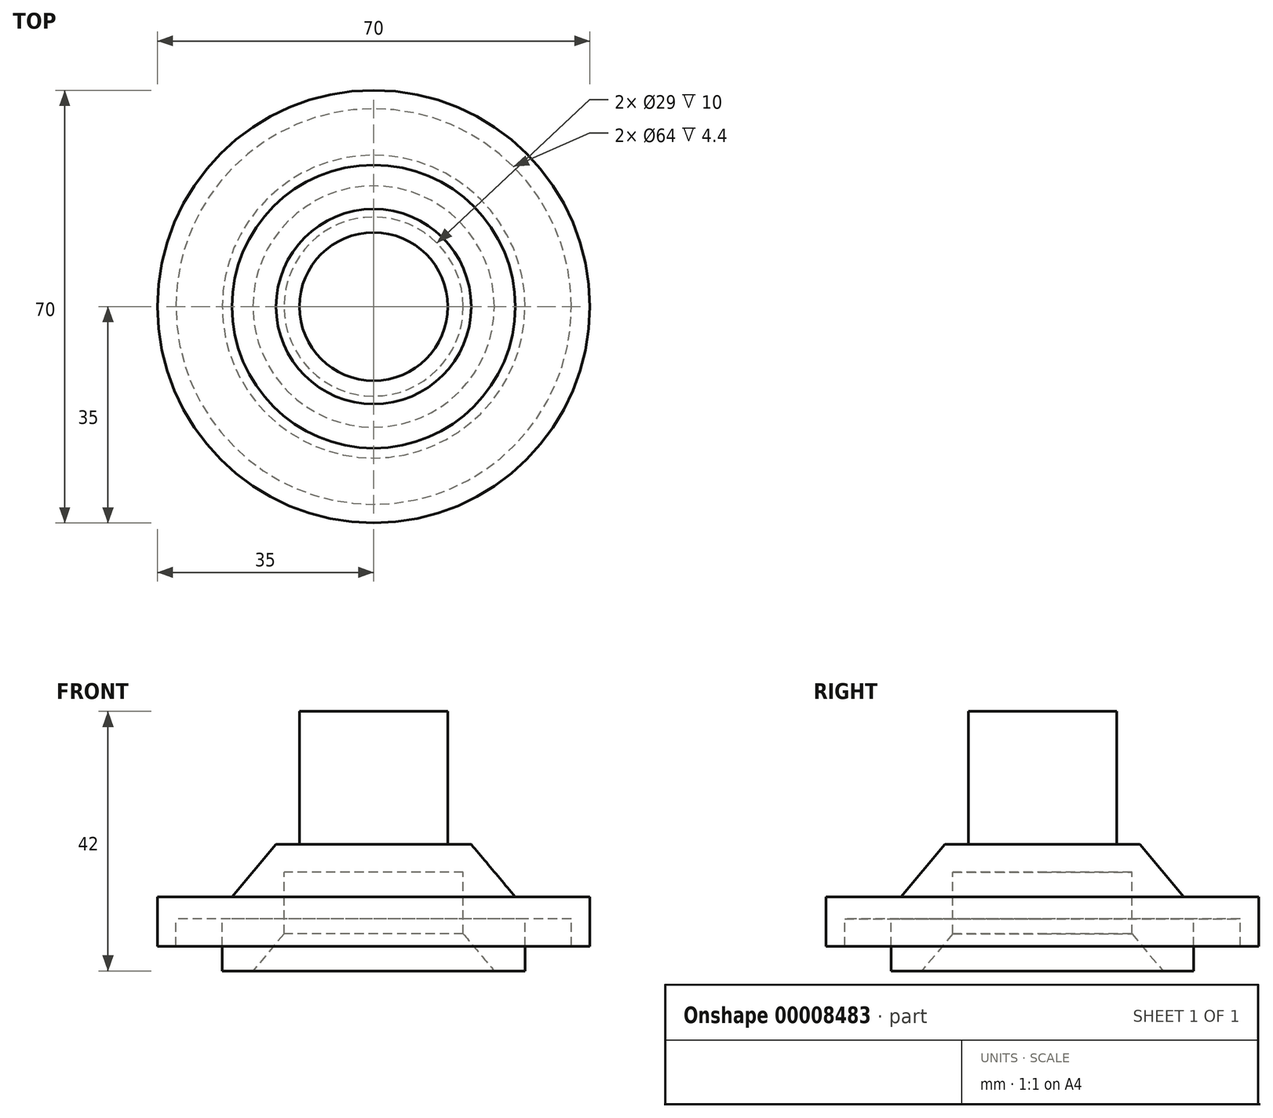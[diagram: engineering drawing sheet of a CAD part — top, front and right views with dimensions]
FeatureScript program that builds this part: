
annotation { "Feature Type Name" : "Feature", "Feature Type Description" : "" }
export const myFeature = defineFeature(function(context is Context, id is Id, definition is map)
    precondition{}
    {
        {
            var Q0;
            Q0=qCreatedBy(makeId("Right.planeOp"),FACE);
            var sketch = newSketch(context, id + "F0", { "sketchPlane" : qUnion([Q0])});
            skLineSegment(sketch, "E0", {"start": v(0, 36) * mm, "end": v(-12, 36) * mm});
            skLineSegment(sketch, "E1", {"start": v(-12, 36) * mm, "end": v(-12, 14.5) * mm});
            skLineSegment(sketch, "E2", {"start": v(-12, 14.5) * mm, "end": v(-15.78, 14.5) * mm});
            skLineSegment(sketch, "E3", {"start": v(-35, -2) * mm, "end": v(-32, -2) * mm});
            skLineSegment(sketch, "E4", {"start": v(-32, -2) * mm, "end": v(-32, 2.4) * mm});
            skLineSegment(sketch, "E5", {"start": v(-32, 2.4) * mm, "end": v(-24.5, 2.4) * mm});
            skLineSegment(sketch, "E6", {"start": v(-24.5, 2.4) * mm, "end": v(-24.5, -6) * mm});
            skLineSegment(sketch, "E7", {"start": v(-24.5, -6) * mm, "end": v(-19.53, -6) * mm});
            skLineSegment(sketch, "E8", {"start": v(-19.53, -6) * mm, "end": v(-14.5, 0) * mm});
            skLineSegment(sketch, "E9", {"start": v(-14.5, 0) * mm, "end": v(-14.5, 10) * mm});
            skLineSegment(sketch, "E10", {"start": v(-14.5, 10) * mm, "end": v(0, 10) * mm});
            skLineSegment(sketch, "E11", {"start": v(0, 36) * mm, "end": v(0, -18.85) * mm, "construction": true});
            skLineSegment(sketch, "E12.0.MirrorCS", {"start": v(32, -2) * mm, "end": v(32, 2.4) * mm});
            skLineSegment(sketch, "E12.1.MirrorCS", {"start": v(35, -2) * mm, "end": v(32, -2) * mm});
            skLineSegment(sketch, "E12.2.MirrorCS", {"start": v(19.53, -6) * mm, "end": v(14.5, 0) * mm});
            skLineSegment(sketch, "E12.3.MirrorCS", {"start": v(14.5, 0) * mm, "end": v(14.5, 10) * mm});
            skLineSegment(sketch, "E12.4.MirrorCS", {"start": v(24.5, 2.4) * mm, "end": v(24.5, -6) * mm});
            skLineSegment(sketch, "E12.5.MirrorCS", {"start": v(24.5, -6) * mm, "end": v(19.53, -6) * mm});
            skLineSegment(sketch, "E12.6.MirrorCS", {"start": v(14.5, 10) * mm, "end": v(0, 10) * mm});
            skLineSegment(sketch, "E12.7.MirrorCS", {"start": v(0, 36) * mm, "end": v(12, 36) * mm});
            skLineSegment(sketch, "E12.8.MirrorCS", {"start": v(32, 2.4) * mm, "end": v(24.5, 2.4) * mm});
            skLineSegment(sketch, "E12.10.MirrorCS", {"start": v(12, 14.5) * mm, "end": v(15.78, 14.5) * mm});
            skLineSegment(sketch, "E12.13.MirrorCS", {"start": v(12, 36) * mm, "end": v(12, 14.5) * mm});
            skLineSegment(sketch, "E13", {"start": v(-35, -2) * mm, "end": v(-35, 6) * mm});
            skLineSegment(sketch, "E14", {"start": v(-35, 6) * mm, "end": v(-22.92, 6) * mm});
            skLineSegment(sketch, "E15", {"start": v(-22.92, 6) * mm, "end": v(-15.78, 14.5) * mm});
            skLineSegment(sketch, "E16", {"start": v(15.78, 14.5) * mm, "end": v(21.58, 6) * mm});
            skLineSegment(sketch, "E17", {"start": v(21.58, 6) * mm, "end": v(35, 6) * mm});
            skLineSegment(sketch, "E18", {"start": v(35, 6) * mm, "end": v(35, -2) * mm});
            skLineSegment(sketch, "E19", {"start": v(0, 36) * mm, "end": v(0, 10) * mm});
            skSolve(sketch);
        }
        {
            var Q0;
            Q0=makeQuery(id+"F0.imprint","IMPRINT",FACE,{"disambiguationData":[TD([[makeQuery(id+"F0.imprint","IMPRINT",EDGE,{"derivedFrom":sQuery(id+"F0.wireOp",EDGE,"E0")}),1.0]])]});
            var Q1;
            Q1=sQuery(id+"F0.wireOp",EDGE,"E19");
            revolve(context, id + "F1", {"entities" : qUnion([Q0]), "axis" : qUnion([Q1]), "revolveType" : RevolveType.FULL});
        }
    });
